# Revit family: Tap_Wall_Nero_Mecca
name_source: partatom
category: Plumbing Fixtures
units: mm (PartAtom-declared; Revit-internal decimal feet)

## family parameters
Always vertical = Yes
Cut with Voids When Loaded = Yes
Maintain Annotation Orientation = No
OmniClass Number = 23.31.11.19
OmniClass Title = Faucet Mixing Valves
Part Type = Normal
Room Calculation Point = No
Round Connector Dimension = Use Diameter
Shared = No
Work Plane-Based = No

## types (7) — shared parameters
Assembly Code = D2010
CW Connection = Yes
Default Elevation = 1050 mm
HW Connection = Yes
IfcExportAs = IfcValve
IfcExportType = MIXING
Manufacturer = Nero
ManufacturerOverallDepth = 64 mm  [stored 0.209974 ft]
ManufacturerOverallHeight = 60 mm  [stored 0.19685 ft]
ManufacturerOverallWidth = 340 mm  [stored 1.11549 ft]
ModifiedIssue = 20251009 $
URL = https://nerotapware.com.au
Uniclass2015Code = Pr_40_20_87
Uniclass2015Title = Taps and water supply outlet fittings
Uniclass2015Version = Products v1.35
Vent Connection = No
Waste Connection = No
zero-valued in all types: CWFU, HWFU, WFU

## per-type parameters (varying)
| type | Description | ManufacturerSpecCode | Material | Model | Type Comments |
| Chrome (25D012CH) | Mecca Wall Top Assemby Chrome | 25D012CH | Metal_Chrome_Nero | 25D012CH | Tap - Wall - Chrome |
| Matte Black (25D012MB) | Mecca Wall Top Assemby Matte Black | 25D012MB | Metal_MatteBlack_Nero | 25D012MB | Tap - Wall - Matte Black |
| Brushed Nickel (25D012BN) | Mecca Wall Top Assemby Brushed Nickel | 25D012BN | Metal_Nickel_Nero_Brushed | 25D012BN | Tap - Wall - Brushed Nickel |
| Gun Metal (25D012GM) | Mecca Wall Top Assemby Gun Metal | 25D012GM | Metal_GunMetal_Nero | 25D012GM | Tap - Wall - Gun Metal |
| Brushed Gold (25D012BG) | Mecca Wall Top Assemby Brushed Gold | 25D012BG | Metal_Gold_Nero_Brushed | 25D012BG | Tap - Wall - Brushed Gold |
| Brushed Bronze (25D012BZ) | Mecca Wall Top Assemby Brushed Bronze | 25D012BZ | Metal_Bronze_Nero_Brushed | 25D012BZ | Tap - Wall - Brushed Bronze |
| Matte White (25D012MW) | Mecca Wall Top Assemby Matte White | 25D012MW | Metal_MatteWhite_Nero | 25D012MW | Tap - Wall - Matte White |

note: [stored X ft] marks values corroborated as IEEE doubles in the binary element streams (Revit-internal decimal feet)

## geometry (parser evidence)
native form markers: Sweep x2
no freeform markers — native parametric forms only
